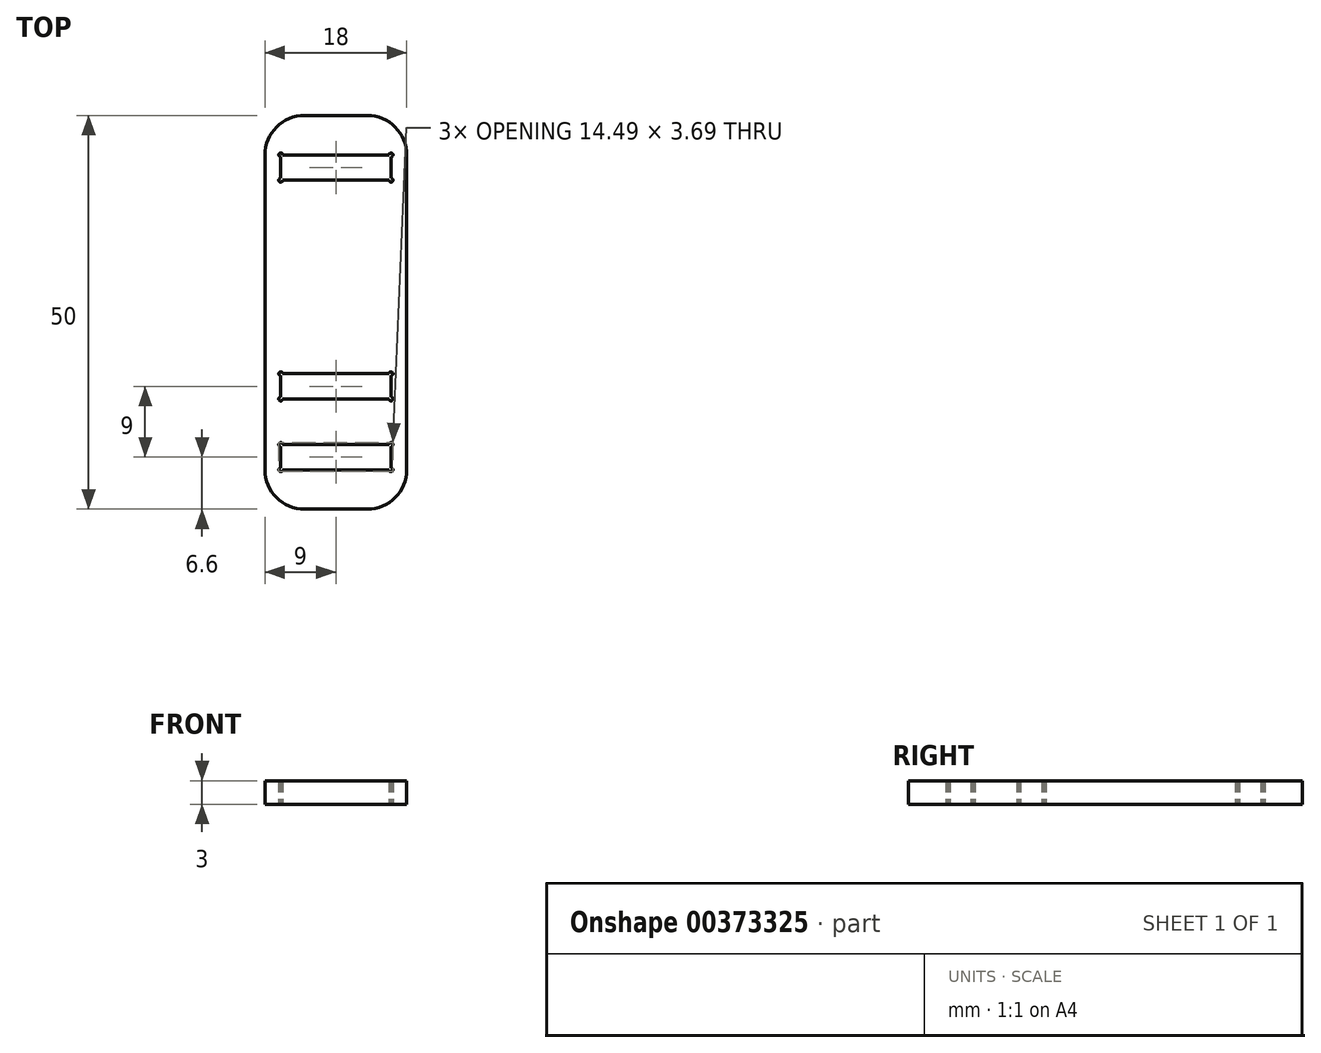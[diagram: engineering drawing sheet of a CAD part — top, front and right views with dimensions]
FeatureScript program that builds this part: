
annotation { "Feature Type Name" : "Feature", "Feature Type Description" : "" }
export const myFeature = defineFeature(function(context is Context, id is Id, definition is map)
    precondition{}
    {
        {
            var Q0;
            Q0=qCreatedBy(makeId("Top.planeOp"),FACE);
            var sketch = newSketch(context, id + "F0", { "sketchPlane" : qUnion([Q0])});
            skLineSegment(sketch, "E0.bottom", {"start": v(-4, 50) * mm, "end": v(4, 50) * mm});
            skLineSegment(sketch, "E0.top", {"start": v(-4, 0) * mm, "end": v(4, 0) * mm});
            skLineSegment(sketch, "E0.left", {"start": v(-9, 45) * mm, "end": v(-9, 5) * mm});
            skLineSegment(sketch, "E0.right", {"start": v(9, 45) * mm, "end": v(9, 5) * mm});
            skLineSegment(sketch, "E1.bottom", {"start": v(-7, 8.2) * mm, "end": v(7, 8.2) * mm});
            skLineSegment(sketch, "E1.top", {"start": v(-7, 5) * mm, "end": v(7, 5) * mm});
            skLineSegment(sketch, "E1.left", {"start": v(-7, 8.2) * mm, "end": v(-7, 5) * mm});
            skLineSegment(sketch, "E1.right", {"start": v(7, 8.2) * mm, "end": v(7, 5) * mm});
            skPoint(sketch, "E2", {"position": v(0, 5) * mm});
            skPoint(sketch, "E3", {"position": v(0, 0) * mm});
            skLineSegment(sketch, "E4", {"start": v(0, 5) * mm, "end": v(0, 0) * mm, "construction": true});
            skCircle(sketch, "E5", {"center": v(-7, 5) * mm, "radius": 0.25 * mm});
            skCircle(sketch, "E6", {"center": v(-7, 8.2) * mm, "radius": 0.25 * mm});
            skCircle(sketch, "E7.MirrorC", {"center": v(7, 5) * mm, "radius": 0.25 * mm});
            skCircle(sketch, "E8.MirrorC", {"center": v(7, 8.2) * mm, "radius": 0.25 * mm});
            skLineSegment(sketch, "E9", {"start": v(-9, 25) * mm, "end": v(9, 25) * mm, "construction": true});
            skLineSegment(sketch, "E10.MirrorCS", {"start": v(7, 5) * mm, "end": v(-7, 5) * mm});
            skLineSegment(sketch, "E11.MirrorCS", {"start": v(7, 8.2) * mm, "end": v(-7, 8.2) * mm});
            skLineSegment(sketch, "E12.MirrorCS", {"start": v(9, 25) * mm, "end": v(-9, 25) * mm, "construction": true});
            skCircle(sketch, "E13.MirrorC", {"center": v(-7, 45) * mm, "radius": 0.25 * mm});
            skLineSegment(sketch, "E14.MirrorCS", {"start": v(7, 45) * mm, "end": v(-7, 45) * mm});
            skCircle(sketch, "E15.MirrorC", {"center": v(-7, 41.8) * mm, "radius": 0.25 * mm});
            skLineSegment(sketch, "E16.MirrorCS", {"start": v(7, 41.8) * mm, "end": v(-7, 41.8) * mm});
            skCircle(sketch, "E17.MirrorC", {"center": v(7, 45) * mm, "radius": 0.25 * mm});
            skCircle(sketch, "E18.MirrorC", {"center": v(7, 41.8) * mm, "radius": 0.25 * mm});
            skLineSegment(sketch, "E19.MirrorCS", {"start": v(-7, 45) * mm, "end": v(7, 45) * mm});
            skLineSegment(sketch, "E20.MirrorCS", {"start": v(-7, 41.8) * mm, "end": v(7, 41.8) * mm});
            skLineSegment(sketch, "E21.MirrorCS", {"start": v(7, 41.8) * mm, "end": v(7, 45) * mm});
            skPoint(sketch, "E22.MirrorP", {"position": v(0, 45) * mm});
            skLineSegment(sketch, "E23.MirrorCS", {"start": v(-7, 41.8) * mm, "end": v(-7, 45) * mm});
            skPoint(sketch, "E24.visualSharp", {"position": v(-9, 50) * mm});
            skArc(sketch, "E24.filletArc", {"start": v(-4, 50) * mm, "mid": v(-7.54, 48.54) * mm, "end": v(-9, 45) * mm});
            skPoint(sketch, "E25.visualSharp", {"position": v(9, 50) * mm});
            skArc(sketch, "E25.filletArc", {"start": v(9, 45) * mm, "mid": v(7.54, 48.54) * mm, "end": v(4, 50) * mm});
            skPoint(sketch, "E26.visualSharp", {"position": v(9, 0) * mm});
            skArc(sketch, "E26.filletArc", {"start": v(4, 0) * mm, "mid": v(7.54, 1.46) * mm, "end": v(9, 5) * mm});
            skPoint(sketch, "E27.visualSharp", {"position": v(-9, 0) * mm});
            skArc(sketch, "E27.filletArc", {"start": v(-9, 5) * mm, "mid": v(-7.54, 1.46) * mm, "end": v(-4, 0) * mm});
            skLineSegment(sketch, "E28.0.1.0", {"start": v(-7, 17.2) * mm, "end": v(7, 17.2) * mm});
            skLineSegment(sketch, "E28.0.1.1", {"start": v(7, 17.2) * mm, "end": v(7, 14) * mm});
            skLineSegment(sketch, "E28.0.1.2", {"start": v(-7, 14) * mm, "end": v(7, 14) * mm});
            skPoint(sketch, "E28.0.1.3", {"position": v(0, 14) * mm});
            skLineSegment(sketch, "E28.0.1.4", {"start": v(-7, 17.2) * mm, "end": v(-7, 14) * mm});
            skLineSegment(sketch, "E28.0.1.5", {"start": v(-7, 17.2) * mm, "end": v(-7, 14) * mm});
            skLineSegment(sketch, "E28.0.1.6", {"start": v(7, 14) * mm, "end": v(-7, 14) * mm});
            skLineSegment(sketch, "E28.0.1.7", {"start": v(7, 17.2) * mm, "end": v(7, 14) * mm});
            skPoint(sketch, "E28.0.1.8", {"position": v(0, 14) * mm});
            skLineSegment(sketch, "E28.0.1.9", {"start": v(7, 17.2) * mm, "end": v(-7, 17.2) * mm});
            skLineSegment(sketch, "E28.0.1.10", {"start": v(-7, 17.2) * mm, "end": v(-7, 14) * mm});
            skPoint(sketch, "E28.0.1.11", {"position": v(0, 14) * mm});
            skLineSegment(sketch, "E28.0.1.12", {"start": v(7, 17.2) * mm, "end": v(7, 14) * mm});
            skLineSegment(sketch, "E28.0.1.13", {"start": v(-7, 14) * mm, "end": v(7, 14) * mm});
            skLineSegment(sketch, "E28.0.1.14", {"start": v(-7, 17.2) * mm, "end": v(7, 17.2) * mm});
            skLineSegment(sketch, "E28.0.1.15", {"start": v(7, 17.2) * mm, "end": v(7, 14) * mm});
            skLineSegment(sketch, "E28.0.1.16", {"start": v(-7, 17.2) * mm, "end": v(-7, 14) * mm});
            skLineSegment(sketch, "E28.0.1.17", {"start": v(7, 17.2) * mm, "end": v(-7, 17.2) * mm});
            skLineSegment(sketch, "E28.0.1.18", {"start": v(7, 14) * mm, "end": v(-7, 14) * mm});
            skPoint(sketch, "E28.0.1.19", {"position": v(0, 14) * mm});
            skCircle(sketch, "E28.0.1.20", {"center": v(7, 17.2) * mm, "radius": 0.25 * mm});
            skCircle(sketch, "E28.0.1.21", {"center": v(7, 14) * mm, "radius": 0.25 * mm});
            skCircle(sketch, "E28.0.1.22", {"center": v(-7, 14) * mm, "radius": 0.25 * mm});
            skCircle(sketch, "E28.0.1.23", {"center": v(-7, 17.2) * mm, "radius": 0.25 * mm});
            skCircle(sketch, "E28.0.1.24", {"center": v(-7, 14) * mm, "radius": 0.25 * mm});
            skCircle(sketch, "E28.0.1.25", {"center": v(7, 14) * mm, "radius": 0.25 * mm});
            skCircle(sketch, "E28.0.1.26", {"center": v(7, 17.2) * mm, "radius": 0.25 * mm});
            skCircle(sketch, "E28.0.1.27", {"center": v(-7, 17.2) * mm, "radius": 0.25 * mm});
            skCircle(sketch, "E28.0.1.28", {"center": v(-7, 14) * mm, "radius": 0.25 * mm});
            skCircle(sketch, "E28.0.1.29", {"center": v(7, 17.2) * mm, "radius": 0.25 * mm});
            skCircle(sketch, "E28.0.1.30", {"center": v(7, 14) * mm, "radius": 0.25 * mm});
            skCircle(sketch, "E28.0.1.31", {"center": v(-7, 17.2) * mm, "radius": 0.25 * mm});
            skCircle(sketch, "E28.0.1.32", {"center": v(7, 17.2) * mm, "radius": 0.25 * mm});
            skCircle(sketch, "E28.0.1.33", {"center": v(-7, 14) * mm, "radius": 0.25 * mm});
            skCircle(sketch, "E28.0.1.34", {"center": v(-7, 17.2) * mm, "radius": 0.25 * mm});
            skCircle(sketch, "E28.0.1.35", {"center": v(7, 14) * mm, "radius": 0.25 * mm});
            skLineSegment(sketch, "E28.direction1", {"start": v(-7, 5) * mm, "end": v(18, 5) * mm, "construction": true});
            skLineSegment(sketch, "E28.direction2", {"start": v(-7, 5) * mm, "end": v(-7, 14) * mm, "construction": true});
            skSolve(sketch);
        }
        {
            var Q0;
            Q0=makeQuery(id+"F0.imprint","IMPRINT",FACE,{"disambiguationData":[TD([[makeQuery(id+"F0.imprint","IMPRINT",EDGE,{"derivedFrom":sQuery(id+"F0.wireOp",EDGE,"E0.bottom")}),-1.0]])]});
            extrude(context, id + "F1", {"entities" : qUnion([Q0]), "depth" : 3 * mm});
        }
    });
